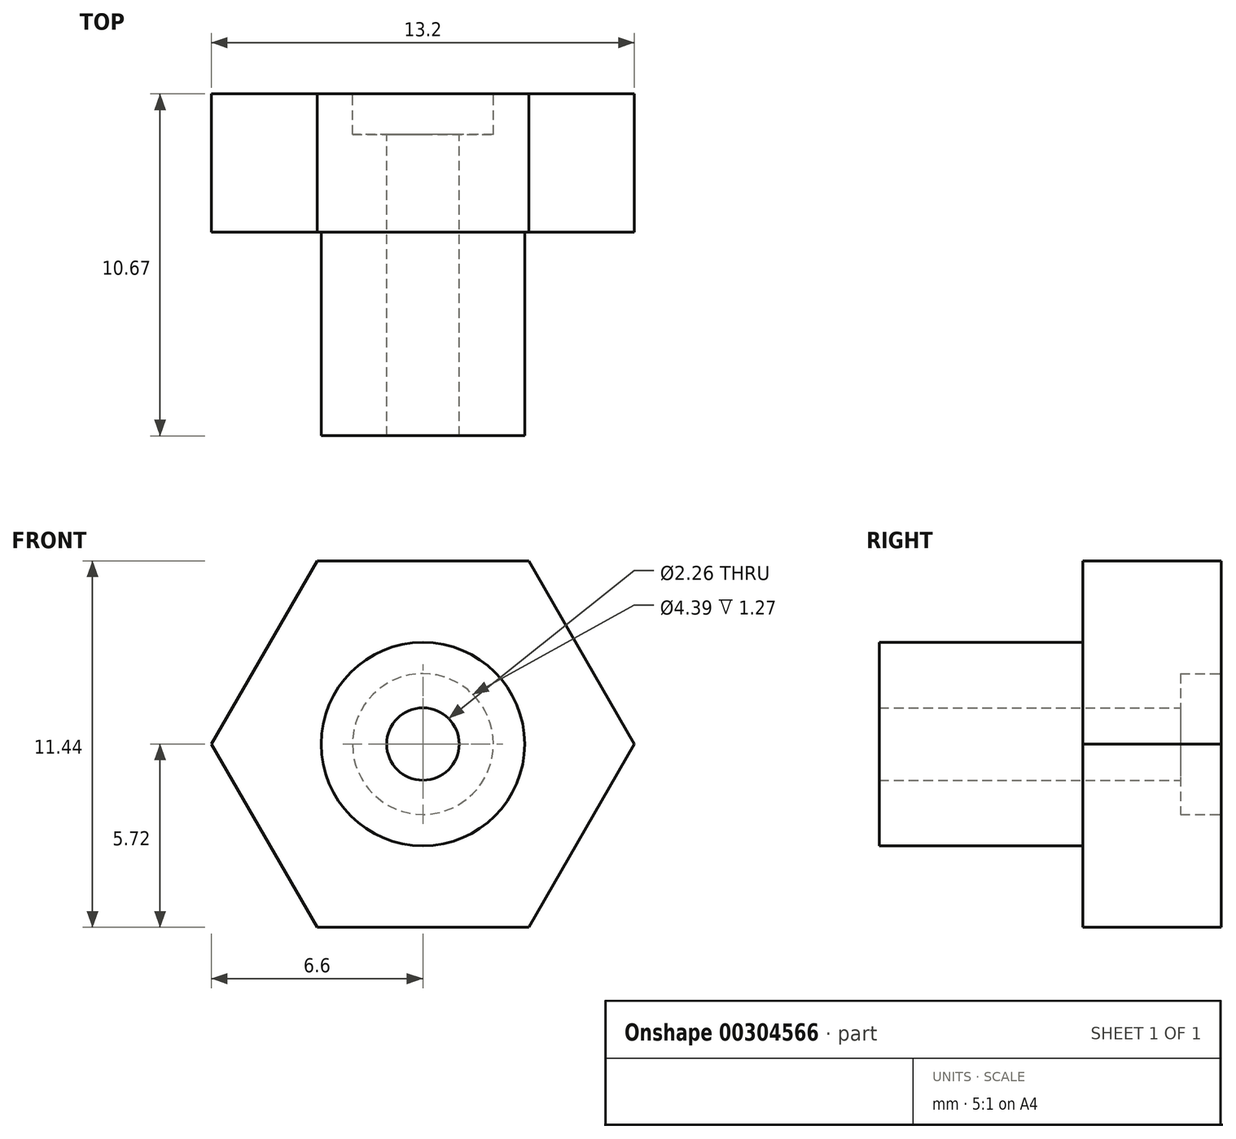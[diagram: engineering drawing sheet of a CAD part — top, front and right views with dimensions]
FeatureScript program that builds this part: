
annotation { "Feature Type Name" : "Feature", "Feature Type Description" : "" }
export const myFeature = defineFeature(function(context is Context, id is Id, definition is map)
    precondition{}
    {
        {
            var Q0;
            Q0=qCreatedBy(makeId("Front.planeOp"),FACE);
            var sketch = newSketch(context, id + "F0", { "sketchPlane" : qUnion([Q0])});
            skCircle(sketch, "E0.cCircle", {"center": v(0, 0) * mm, "radius": 5.72 * mm, "construction": true});
            skLineSegment(sketch, "E0.0", {"start": v(-3.3, 5.72) * mm, "end": v(3.3, 5.72) * mm});
            skLineSegment(sketch, "E0.1", {"start": v(3.3, 5.72) * mm, "end": v(6.6, 0) * mm});
            skLineSegment(sketch, "E0.2", {"start": v(6.6, 0) * mm, "end": v(3.3, -5.71) * mm});
            skLineSegment(sketch, "E0.3", {"start": v(3.3, -5.71) * mm, "end": v(-3.3, -5.72) * mm});
            skLineSegment(sketch, "E0.4", {"start": v(-3.3, -5.72) * mm, "end": v(-6.6, 0) * mm});
            skLineSegment(sketch, "E0.5", {"start": v(-6.6, 0) * mm, "end": v(-3.3, 5.72) * mm});
            skPoint(sketch, "E0.0.midPoint", {"position": v(0, 5.72) * mm});
            skSolve(sketch);
        }
        {
            var Q0;
            Q0=makeQuery(id+"F0.imprint","IMPRINT",FACE,{"disambiguationData":[TD([[makeQuery(id+"F0.imprint","IMPRINT",EDGE,{"derivedFrom":sQuery(id+"F0.wireOp",EDGE,"E0.0")}),-1.0]])]});
            extrude(context, id + "F1", {"entities" : qUnion([Q0]), "depth" : 4.32 * mm});
        }
        {
            var Q0;
            Q0=makeQuery(id+"F1.opExtrude","CAP_FACE",FACE,{"disambiguationData":[OSD([sQuery(id+"F0.wireOp",EDGE,"E0.0"),sQuery(id+"F0.wireOp",EDGE,"E0.1"),sQuery(id+"F0.wireOp",EDGE,"E0.2"),sQuery(id+"F0.wireOp",EDGE,"E0.3"),sQuery(id+"F0.wireOp",EDGE,"E0.4"),sQuery(id+"F0.wireOp",EDGE,"E0.5")])],"isStart":false});
            var sketch = newSketch(context, id + "F2", { "sketchPlane" : qUnion([Q0])});
            skCircle(sketch, "E1", {"center": v(0, 0) * mm, "radius": 1.13 * mm});
            skCircle(sketch, "E2", {"center": v(0, 0) * mm, "radius": 3.18 * mm});
            skSolve(sketch);
        }
        {
            var Q0;
            Q0=makeQuery(id+"F2.imprint","IMPRINT",FACE,{"disambiguationData":[TD([[makeQuery(id+"F2.imprint","IMPRINT",EDGE,{"derivedFrom":sQuery(id+"F2.wireOp",EDGE,"E1")}),-1.0]])]});
            extrude(context, id + "F3", {"entities" : qUnion([Q0]), "operationType" : NewBodyOperationType.ADD, "depth" : 6.35 * mm});
        }
        {
            var Q0;
            Q0=makeQuery(id+"F1.opExtrude","CAP_FACE",FACE,{"disambiguationData":[OSD([sQuery(id+"F0.wireOp",EDGE,"E0.0"),sQuery(id+"F0.wireOp",EDGE,"E0.1"),sQuery(id+"F0.wireOp",EDGE,"E0.2"),sQuery(id+"F0.wireOp",EDGE,"E0.3"),sQuery(id+"F0.wireOp",EDGE,"E0.4"),sQuery(id+"F0.wireOp",EDGE,"E0.5")])],"isStart":true});
            var sketch = newSketch(context, id + "F4", { "sketchPlane" : qUnion([Q0])});
            skCircle(sketch, "E3", {"center": v(0, 0) * mm, "radius": 2.2 * mm});
            skSolve(sketch);
        }
        {
            var Q0;
            Q0=makeQuery(id+"F4.imprint","IMPRINT",FACE,{"disambiguationData":[TD([[makeQuery(id+"F4.imprint","IMPRINT",EDGE,{"derivedFrom":sQuery(id+"F4.wireOp",EDGE,"E3")}),1.0]])]});
            extrude(context, id + "F5", {"entities" : qUnion([Q0]), "operationType" : NewBodyOperationType.REMOVE, "oppositeDirection" : true, "depth" : 1.27 * mm});
        }
        {
            var Q0;
            Q0=makeQuery(id+"F5.boolean.opBoolean","COPY",FACE,{"derivedFrom":makeQuery(id+"F5.opExtrude","CAP_FACE",FACE,{"disambiguationData":[OSD([sQuery(id+"F4.wireOp",EDGE,"E3")])],"isStart":false})});
            var sketch = newSketch(context, id + "F6", { "sketchPlane" : qUnion([Q0])});
            skCircle(sketch, "E4", {"center": v(0, 0) * mm, "radius": 1.13 * mm});
            skSolve(sketch);
        }
        {
            var Q0;
            Q0=makeQuery(id+"F6.imprint","IMPRINT",FACE,{"disambiguationData":[TD([[makeQuery(id+"F6.imprint","IMPRINT",EDGE,{"derivedFrom":sQuery(id+"F6.wireOp",EDGE,"E4")}),1.0]])]});
            extrude(context, id + "F7", {"entities" : qUnion([Q0]), "operationType" : NewBodyOperationType.REMOVE, "oppositeDirection" : true, "depth" : 25.4 * mm});
        }
    });
